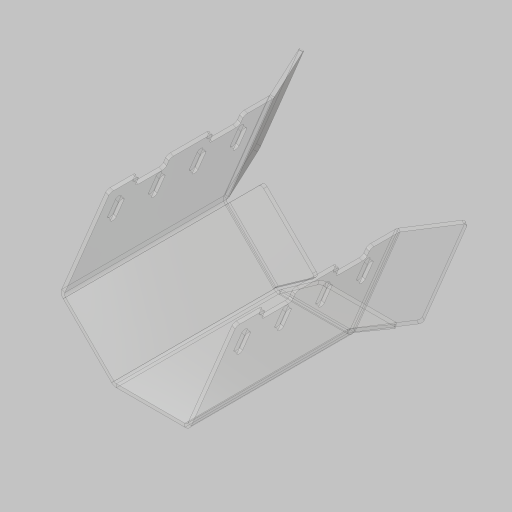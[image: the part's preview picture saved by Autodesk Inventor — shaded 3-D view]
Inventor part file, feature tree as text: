
AUTODESK INVENTOR PART (.ipt)
format: ipt  version: 2023.5 (Build 275446000, 446)  size: 349,696 bytes
history: native  units: in
note: dims shown in document units (in); Inventor stores cm internally (conversion verified against a paired STEP export)
features: sheet_metal_op x11, sketch x7, other x4, extrude x2, fillet x1, projected_geometry x1
ambient origin geometry x8: Origin, YZ Plane, XZ Plane, XY Plane, X Axis, Y Axis, Z Axis, Center Point
bodies: Solid1 (feature_tree)
feature tree (26):
  sheet_metal_op  "Face1"
  sheet_metal_op  "Fold1"
  sheet_metal_op  "Flange1"
  sheet_metal_op  "Flange2"
  sheet_metal_op  "Flange3"
  extrude  "Extrusion1"  Depth=6.0in
  extrude  "Extrusion2"  Depth=0.125in
  fillet  "Fillet1"  Radius=0.0625in
  sketch  "Sketch1"  dims[d0=5.5in d1=6.0in]
  other  "Plate1"
  sketch  "Sketch2"  dims[d2=0.125in d3=0.125in d4=0.0625in]
  sketch  "Sketch3"  dims[d5=0.25in]
  other  "Plate2"
  sheet_metal_op  "Bend1"
  sheet_metal_op  "Corner1"
  sketch  "Sketch4"  dims[d6=0.125in]
  other  "Plate3"
  sheet_metal_op  "Bend2"
  sheet_metal_op  "Corner2"
  sketch  "Sketch5"  dims[d7=45.0deg d8=0.125in]
  other  "Plate4"
  sheet_metal_op  "Bend3"
  sheet_metal_op  "Corner3"
  sketch  "Sketch7"  dims[d9=0.125in]
  sketch  "Sketch8"  dims[d10=0.0625in d11=0.25in d12=0.125in d13=4.5in d14=67.5deg d15=0.125in d16=0.5in d17=0.125in d18=0.125in d19=0.125in d20=0.0625in d21=0.25in d22=0.125in d23=4.5in d24=67.5deg d25=0.125in d26=0.5in d27=0.125in d28=0.125in d29=0.125in d30=0.0625in d31=0.25in d32=0.125in d33=2.0in d34=22.5deg d35=0.125in d36=0.5in d37=0.125in d38=0.125in d50=0.201in d51=1.25in d53=0.75in d54=1.5748in d56=1.5in d57=0.3937in d59=1.0in d61=0.0in d62=0.0in d63=0.75in d64=1.125in d66=0.25in d67=0.7in d68=0.0in d69=0.0in d70=0.892in d71=0.125in]
  projected_geometry  "Project Cut Edges1"
